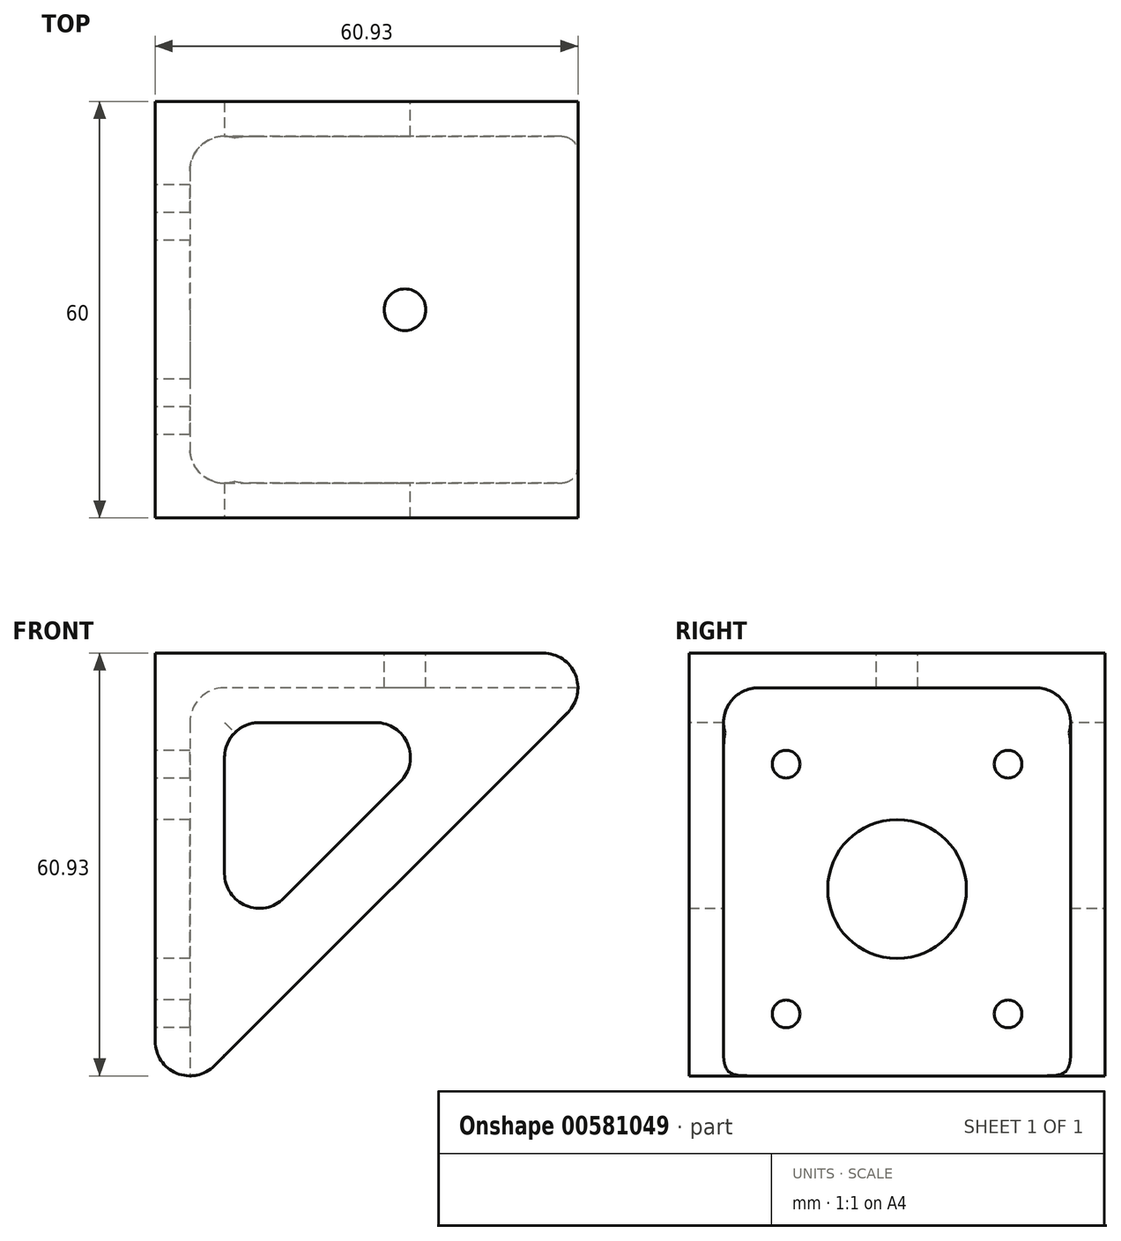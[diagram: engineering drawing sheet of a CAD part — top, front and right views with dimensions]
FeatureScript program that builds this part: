
annotation { "Feature Type Name" : "Feature", "Feature Type Description" : "" }
export const myFeature = defineFeature(function(context is Context, id is Id, definition is map)
    precondition{}
    {
        {
            var Q0;
            Q0=qCreatedBy(makeId("Right.planeOp"),FACE);
            var sketch = newSketch(context, id + "F0", { "sketchPlane" : qUnion([Q0])});
            skLineSegment(sketch, "E0.bottom", {"start": v(30, 34) * mm, "end": v(-30, 34) * mm});
            skLineSegment(sketch, "E0.top", {"start": v(30, -34) * mm, "end": v(-30, -34) * mm});
            skLineSegment(sketch, "E0.left", {"start": v(30, 34) * mm, "end": v(30, -34) * mm});
            skLineSegment(sketch, "E0.right", {"start": v(-30, 34) * mm, "end": v(-30, -34) * mm});
            skPoint(sketch, "E0.middle", {"position": v(0, 0) * mm});
            skCircle(sketch, "E1", {"center": v(-16, 18) * mm, "radius": 2 * mm});
            skCircle(sketch, "E2.MirrorC", {"center": v(16, 18) * mm, "radius": 2 * mm});
            skCircle(sketch, "E3.MirrorC", {"center": v(16, -18) * mm, "radius": 2 * mm});
            skCircle(sketch, "E4.MirrorC", {"center": v(-16, -18) * mm, "radius": 2 * mm});
            skLineSegment(sketch, "E5", {"start": v(-25, -34) * mm, "end": v(-25, 29) * mm});
            skLineSegment(sketch, "E6", {"start": v(-25, 29) * mm, "end": v(0, 29) * mm});
            skLineSegment(sketch, "E7.MirrorCS", {"start": v(25, 29) * mm, "end": v(0, 29) * mm});
            skLineSegment(sketch, "E8.MirrorCS", {"start": v(25, -34) * mm, "end": v(25, 29) * mm});
            skLineSegment(sketch, "E9", {"start": v(-25, 29) * mm, "end": v(-30, 29) * mm});
            skLineSegment(sketch, "E10.MirrorCS", {"start": v(25, 29) * mm, "end": v(30, 29) * mm});
            skSolve(sketch);
        }
        {
            var Q0;
            Q0=makeQuery(id+"F0.imprint","IMPRINT",FACE,{"disambiguationData":[TD([[makeQuery(id+"F0.imprint","IMPRINT",EDGE,{"derivedFrom":sQuery(id+"F0.wireOp",EDGE,"E0.bottom")}),1.0]])]});
            var Q1;
            Q1=makeQuery(id+"F0.imprint","IMPRINT",FACE,{"disambiguationData":[TD([[makeQuery(id+"F0.imprint","IMPRINT",EDGE,{"derivedFrom":sQuery(id+"F0.wireOp",EDGE,"E1")}),-1.0]])]});
            var Q2;
            {var subQ3=sQuery(id+"F0.wireOp",EDGE,"E5");Q2=makeQuery(id+"F0.imprint","IMPRINT",FACE,{"disambiguationData":[TD([[makeQuery(id+"F0.imprint","IMPRINT",EDGE,{"derivedFrom":subQ3}),1.0]])]});}
            var Q3;
            {var subQ3=sQuery(id+"F0.wireOp",EDGE,"E8.MirrorCS");Q3=makeQuery(id+"F0.imprint","IMPRINT",FACE,{"disambiguationData":[TD([[makeQuery(id+"F0.imprint","IMPRINT",EDGE,{"derivedFrom":subQ3}),-1.0]])]});}
            extrude(context, id + "F1", {"entities" : qUnion([Q0, Q1, Q2, Q3]), "depth" : 5 * mm, "offsetDistance" : 25 * mm});
        }
        {
            var Q0;
            {var subQ3=sQuery(id+"F0.wireOp",EDGE,"E5");Q0=makeQuery(id+"F0.imprint","IMPRINT",FACE,{"disambiguationData":[TD([[makeQuery(id+"F0.imprint","IMPRINT",EDGE,{"derivedFrom":subQ3}),1.0]])]});}
            var Q1;
            {var subQ3=sQuery(id+"F0.wireOp",EDGE,"E8.MirrorCS");Q1=makeQuery(id+"F0.imprint","IMPRINT",FACE,{"disambiguationData":[TD([[makeQuery(id+"F0.imprint","IMPRINT",EDGE,{"derivedFrom":subQ3}),-1.0]])]});}
            var Q2;
            {var subQ1=sQuery(id+"F0.wireOp",EDGE,"E0.bottom");Q2=makeQuery(id+"F0.imprint","IMPRINT",FACE,{"disambiguationData":[TD([[makeQuery(id+"F0.imprint","IMPRINT",EDGE,{"derivedFrom":subQ1}),1.0]])]});}
            extrude(context, id + "F2", {"entities" : qUnion([Q0, Q1, Q2]), "operationType" : NewBodyOperationType.ADD, "depth" : 72 * mm, "offsetDistance" : 25 * mm});
        }
        {
            var Q0;
            {var subQ0=sQuery(id+"F0.wireOp",EDGE,"E0.top");Q0=makeQuery(id+"F2.opExtrude","CAP_EDGE",EDGE,{"disambiguationData":[OSD([subQ0]),TDD([makeQuery(id+"F0.imprint","IMPRINT",EDGE,{"disambiguationData":[TD([[makeQuery(id+"F0.imprint","INTERSECT",VERTEX,{"derivedFrom":[subQ0,sQuery(id+"F0.wireOp",EDGE,"E0.right")]}),1.0]])],"derivedFrom":subQ0})])],"isStart":false});}
            chamfer(context, id + "F3", {"entities" : qUnion([Q0]), "width" : 72 * mm, "tangentPropagation" : true});
        }
        {
            var Q0;
            Q0=makeQuery(id+"F2.boolean.opBoolean","INTERSECT",EDGE,{"derivedFrom":[makeQuery(id+"F1.opExtrude","CAP_FACE",FACE,{"disambiguationData":[OSD([sQuery(id+"F0.wireOp",EDGE,"E0.bottom"),sQuery(id+"F0.wireOp",EDGE,"E0.top"),sQuery(id+"F0.wireOp",EDGE,"E0.left"),sQuery(id+"F0.wireOp",EDGE,"E0.right"),sQuery(id+"F0.wireOp",EDGE,"E1"),sQuery(id+"F0.wireOp",EDGE,"E2.MirrorC"),sQuery(id+"F0.wireOp",EDGE,"E3.MirrorC"),sQuery(id+"F0.wireOp",EDGE,"E4.MirrorC")])],"isStart":false}),makeQuery(id+"F2.opExtrude","SWEPT_FACE",FACE,{"disambiguationData":[OSD([sQuery(id+"F0.wireOp",EDGE,"E5")])]})]});
            var Q1;
            Q1=makeQuery(id+"F2.boolean.opBoolean","INTERSECT",EDGE,{"derivedFrom":[makeQuery(id+"F1.opExtrude","CAP_FACE",FACE,{"disambiguationData":[OSD([sQuery(id+"F0.wireOp",EDGE,"E0.bottom"),sQuery(id+"F0.wireOp",EDGE,"E0.top"),sQuery(id+"F0.wireOp",EDGE,"E0.left"),sQuery(id+"F0.wireOp",EDGE,"E0.right"),sQuery(id+"F0.wireOp",EDGE,"E1"),sQuery(id+"F0.wireOp",EDGE,"E2.MirrorC"),sQuery(id+"F0.wireOp",EDGE,"E3.MirrorC"),sQuery(id+"F0.wireOp",EDGE,"E4.MirrorC")])],"isStart":false}),makeQuery(id+"F2.opExtrude","SWEPT_FACE",FACE,{"disambiguationData":[OSD([sQuery(id+"F0.wireOp",EDGE,"E8.MirrorCS")])]})]});
            var Q2;
            Q2=makeQuery(id+"F2.boolean.opBoolean","INTERSECT",EDGE,{"derivedFrom":[makeQuery(id+"F1.opExtrude","CAP_FACE",FACE,{"disambiguationData":[OSD([sQuery(id+"F0.wireOp",EDGE,"E0.bottom"),sQuery(id+"F0.wireOp",EDGE,"E0.top"),sQuery(id+"F0.wireOp",EDGE,"E0.left"),sQuery(id+"F0.wireOp",EDGE,"E0.right"),sQuery(id+"F0.wireOp",EDGE,"E1"),sQuery(id+"F0.wireOp",EDGE,"E2.MirrorC"),sQuery(id+"F0.wireOp",EDGE,"E3.MirrorC"),sQuery(id+"F0.wireOp",EDGE,"E4.MirrorC")])],"isStart":false}),makeQuery(id+"F2.opExtrude","SWEPT_FACE",FACE,{"disambiguationData":[OSD([sQuery(id+"F0.wireOp",EDGE,"E6"),sQuery(id+"F0.wireOp",EDGE,"E7.MirrorCS")])]})]});
            var Q3;
            Q3=makeQuery(id+"F2.opExtrude","SWEPT_EDGE",EDGE,{"disambiguationData":[OSD([sQuery(id+"F0.wireOp",EDGE,"E7.MirrorCS"),sQuery(id+"F0.wireOp",EDGE,"E8.MirrorCS"),sQuery(id+"F0.wireOp",EDGE,"E10.MirrorCS")])]});
            var Q4;
            Q4=makeQuery(id+"F2.opExtrude","SWEPT_EDGE",EDGE,{"disambiguationData":[OSD([sQuery(id+"F0.wireOp",EDGE,"E5"),sQuery(id+"F0.wireOp",EDGE,"E6"),sQuery(id+"F0.wireOp",EDGE,"E9")])]});
            fillet(context, id + "F4", {"entities" : qUnion([Q0, Q1, Q2, Q3, Q4]), "radius" : 5 * mm, "tangentPropagation" : true, "allowEdgeOverflow" : false});
        }
        {
            var Q0;
            {var subQ0=sQuery(id+"F0.wireOp",EDGE,"E0.bottom");var subQ1=sQuery(id+"F0.wireOp",EDGE,"E0.top");Q0=makeQuery(id+"F3.opChamfer","BLEND_EDGE",EDGE,{"blendedFrom":[makeQuery(id+"F2.opExtrude","CAP_EDGE",EDGE,{"disambiguationData":[OSD([subQ1]),TDD([makeQuery(id+"F0.imprint","IMPRINT",EDGE,{"disambiguationData":[TD([[makeQuery(id+"F0.imprint","INTERSECT",VERTEX,{"derivedFrom":[subQ1,sQuery(id+"F0.wireOp",EDGE,"E0.right")]}),1.0]])],"derivedFrom":subQ1})])],"isStart":false}),makeQuery(id+"F2.boolean.opBoolean","MERGE",FACE,{"derivedFrom":[makeQuery(id+"F1.opExtrude","SWEPT_FACE",FACE,{"disambiguationData":[OSD([subQ0])]}),makeQuery(id+"F2.opExtrude","SWEPT_FACE",FACE,{"disambiguationData":[OSD([subQ0])]})]})],"blendedInto":[makeQuery(id+"F2.boolean.opBoolean","MERGE",FACE,{"derivedFrom":[makeQuery(id+"F1.opExtrude","SWEPT_FACE",FACE,{"disambiguationData":[OSD([subQ0])]}),makeQuery(id+"F2.opExtrude","SWEPT_FACE",FACE,{"disambiguationData":[OSD([subQ0])]})]})]});}
            var Q1;
            {var subQ0=sQuery(id+"F0.wireOp",EDGE,"E0.right");var subQ1=sQuery(id+"F0.wireOp",EDGE,"E0.top");Q1=makeQuery(id+"F3.opChamfer","BLEND_EDGE",EDGE,{"blendedFrom":[makeQuery(id+"F2.opExtrude","CAP_EDGE",EDGE,{"disambiguationData":[OSD([subQ1]),TDD([makeQuery(id+"F0.imprint","IMPRINT",EDGE,{"disambiguationData":[TD([[makeQuery(id+"F0.imprint","INTERSECT",VERTEX,{"derivedFrom":[subQ1,subQ0]}),1.0]])],"derivedFrom":subQ1})])],"isStart":false}),makeQuery(id+"F1.opExtrude","CAP_FACE",FACE,{"disambiguationData":[OSD([sQuery(id+"F0.wireOp",EDGE,"E0.bottom"),subQ1,sQuery(id+"F0.wireOp",EDGE,"E0.left"),subQ0,sQuery(id+"F0.wireOp",EDGE,"E1"),sQuery(id+"F0.wireOp",EDGE,"E2.MirrorC"),sQuery(id+"F0.wireOp",EDGE,"E3.MirrorC"),sQuery(id+"F0.wireOp",EDGE,"E4.MirrorC")])],"isStart":true})],"blendedInto":[makeQuery(id+"F1.opExtrude","CAP_FACE",FACE,{"disambiguationData":[OSD([sQuery(id+"F0.wireOp",EDGE,"E0.bottom"),subQ1,sQuery(id+"F0.wireOp",EDGE,"E0.left"),subQ0,sQuery(id+"F0.wireOp",EDGE,"E1"),sQuery(id+"F0.wireOp",EDGE,"E2.MirrorC"),sQuery(id+"F0.wireOp",EDGE,"E3.MirrorC"),sQuery(id+"F0.wireOp",EDGE,"E4.MirrorC")])],"isStart":true})]});}
            fillet(context, id + "F5", {"entities" : qUnion([Q0, Q1]), "radius" : 5 * mm, "tangentPropagation" : true, "allowEdgeOverflow" : false});
        }
        {
            var Q0;
            {var subQ0=sQuery(id+"F0.wireOp",EDGE,"E0.bottom");Q0=makeQuery(id+"F2.boolean.opBoolean","MERGE",FACE,{"derivedFrom":[makeQuery(id+"F1.opExtrude","SWEPT_FACE",FACE,{"disambiguationData":[OSD([subQ0])]}),makeQuery(id+"F2.opExtrude","SWEPT_FACE",FACE,{"disambiguationData":[OSD([subQ0])]})]});}
            var sketch = newSketch(context, id + "F6", { "sketchPlane" : qUnion([Q0])});
            skCircle(sketch, "E11", {"center": v(36, 0) * mm, "radius": 3 * mm});
            skSolve(sketch);
        }
        {
            var Q0;
            Q0 = qSketchRegion(id + "F6", true);
            extrude(context, id + "F7", {"entities" : qUnion([Q0]), "operationType" : NewBodyOperationType.REMOVE, "oppositeDirection" : true, "depth" : 25 * mm, "offsetDistance" : 25 * mm});
        }
        {
            var Q0;
            {var subQ0=sQuery(id+"F0.wireOp",EDGE,"E0.right");Q0=makeQuery(id+"F2.boolean.opBoolean","MERGE",FACE,{"derivedFrom":[makeQuery(id+"F1.opExtrude","SWEPT_FACE",FACE,{"disambiguationData":[OSD([subQ0])]}),makeQuery(id+"F2.opExtrude","SWEPT_FACE",FACE,{"disambiguationData":[OSD([subQ0])]})]});}
            var sketch = newSketch(context, id + "F8", { "sketchPlane" : qUnion([Q0])});
            skLineSegment(sketch, "E12.1", {"start": v(1.74, -18.12) * mm, "end": v(52.12, 32.26) * mm});
            skLineSegment(sketch, "E12.2", {"start": v(55.54, 24) * mm, "end": v(10, 24) * mm});
            skLineSegment(sketch, "E12.3", {"start": v(10, 24) * mm, "end": v(10, -21.54) * mm});
            skSolve(sketch);
        }
        {
            var Q0;
            Q0 = qSketchRegion(id + "F8", true);
            extrude(context, id + "F9", {"entities" : qUnion([Q0]), "operationType" : NewBodyOperationType.REMOVE, "endBound" : BoundingType.THROUGH_ALL, "oppositeDirection" : true, "depth" : 25 * mm, "offsetDistance" : 25 * mm});
        }
        {
            var Q0;
            {var subQ4=sQuery(id+"F0.wireOp",EDGE,"E0.right");var subQ8=sQuery(id+"F8.wireOp",EDGE,"E12.1");var subQ9=sQuery(id+"F8.wireOp",EDGE,"E12.3");Q0=makeQuery(id+"F9.boolean.opBoolean","COPY",EDGE,{"disambiguationData":[TD([makeQuery(id+"F1.opExtrude","SWEPT_FACE",FACE,{"disambiguationData":[OSD([subQ4])]})])],"derivedFrom":makeQuery(id+"F9.opExtrude","SWEPT_EDGE",EDGE,{"disambiguationData":[OSD([subQ8,subQ9])]})});}
            var Q1;
            {var subQ1=sQuery(id+"F0.wireOp",EDGE,"E0.right");var subQ2=sQuery(id+"F8.wireOp",EDGE,"E12.1");var subQ3=sQuery(id+"F8.wireOp",EDGE,"E12.2");Q1=makeQuery(id+"F9.boolean.opBoolean","COPY",EDGE,{"disambiguationData":[TD([makeQuery(id+"F1.opExtrude","SWEPT_FACE",FACE,{"disambiguationData":[OSD([subQ1])]})])],"derivedFrom":makeQuery(id+"F9.opExtrude","SWEPT_EDGE",EDGE,{"disambiguationData":[OSD([subQ2,subQ3])]})});}
            var Q2;
            {var subQ5=sQuery(id+"F0.wireOp",EDGE,"E0.left");var subQ8=sQuery(id+"F8.wireOp",EDGE,"E12.1");var subQ9=sQuery(id+"F8.wireOp",EDGE,"E12.3");Q2=makeQuery(id+"F9.boolean.opBoolean","COPY",EDGE,{"disambiguationData":[TD([makeQuery(id+"F1.opExtrude","SWEPT_FACE",FACE,{"disambiguationData":[OSD([subQ5])]})])],"derivedFrom":makeQuery(id+"F9.opExtrude","SWEPT_EDGE",EDGE,{"disambiguationData":[OSD([subQ8,subQ9])]})});}
            var Q3;
            {var subQ1=sQuery(id+"F8.wireOp",EDGE,"E12.1");var subQ2=sQuery(id+"F0.wireOp",EDGE,"E0.left");var subQ3=sQuery(id+"F8.wireOp",EDGE,"E12.2");Q3=makeQuery(id+"F9.boolean.opBoolean","COPY",EDGE,{"disambiguationData":[TD([makeQuery(id+"F1.opExtrude","SWEPT_FACE",FACE,{"disambiguationData":[OSD([subQ2])]})])],"derivedFrom":makeQuery(id+"F9.opExtrude","SWEPT_EDGE",EDGE,{"disambiguationData":[OSD([subQ1,subQ3])]})});}
            fillet(context, id + "F10", {"entities" : qUnion([Q0, Q1, Q2, Q3]), "radius" : 5 * mm, "tangentPropagation" : true, "allowEdgeOverflow" : false});
        }
        {
            var Q0;
            Q0=makeQuery(id+"F1.opExtrude","CAP_FACE",FACE,{"disambiguationData":[OSD([sQuery(id+"F0.wireOp",EDGE,"E0.bottom"),sQuery(id+"F0.wireOp",EDGE,"E0.top"),sQuery(id+"F0.wireOp",EDGE,"E0.left"),sQuery(id+"F0.wireOp",EDGE,"E0.right"),sQuery(id+"F0.wireOp",EDGE,"E1"),sQuery(id+"F0.wireOp",EDGE,"E2.MirrorC"),sQuery(id+"F0.wireOp",EDGE,"E3.MirrorC"),sQuery(id+"F0.wireOp",EDGE,"E4.MirrorC")])],"isStart":true});
            var sketch = newSketch(context, id + "F11", { "sketchPlane" : qUnion([Q0])});
            skCircle(sketch, "E13", {"center": v(0, 0) * mm, "radius": 10 * mm});
            skSolve(sketch);
        }
        {
            var Q0;
            Q0 = qSketchRegion(id + "F11", true);
            extrude(context, id + "F12", {"entities" : qUnion([Q0]), "operationType" : NewBodyOperationType.REMOVE, "endBound" : BoundingType.UP_TO_NEXT, "oppositeDirection" : true, "depth" : 25 * mm, "offsetDistance" : 25 * mm});
        }
        {
            var Q0;
            {var subQ7=sQuery(id+"F0.wireOp",EDGE,"E0.left");var subQ10=sQuery(id+"F8.wireOp",EDGE,"E12.2");var subQ11=sQuery(id+"F8.wireOp",EDGE,"E12.3");Q0=makeQuery(id+"F9.boolean.opBoolean","COPY",EDGE,{"disambiguationData":[TD([makeQuery(id+"F1.opExtrude","SWEPT_FACE",FACE,{"disambiguationData":[OSD([subQ7])]})])],"derivedFrom":makeQuery(id+"F9.opExtrude","SWEPT_EDGE",EDGE,{"disambiguationData":[OSD([subQ10,subQ11])]})});}
            var Q1;
            {var subQ6=sQuery(id+"F0.wireOp",EDGE,"E0.right");var subQ10=sQuery(id+"F8.wireOp",EDGE,"E12.2");var subQ11=sQuery(id+"F8.wireOp",EDGE,"E12.3");Q1=makeQuery(id+"F9.boolean.opBoolean","COPY",EDGE,{"disambiguationData":[TD([makeQuery(id+"F1.opExtrude","SWEPT_FACE",FACE,{"disambiguationData":[OSD([subQ6])]})])],"derivedFrom":makeQuery(id+"F9.opExtrude","SWEPT_EDGE",EDGE,{"disambiguationData":[OSD([subQ10,subQ11])]})});}
            fillet(context, id + "F13", {"entities" : qUnion([Q0, Q1]), "radius" : 5 * mm, "tangentPropagation" : true, "allowEdgeOverflow" : false});
        }
    });
